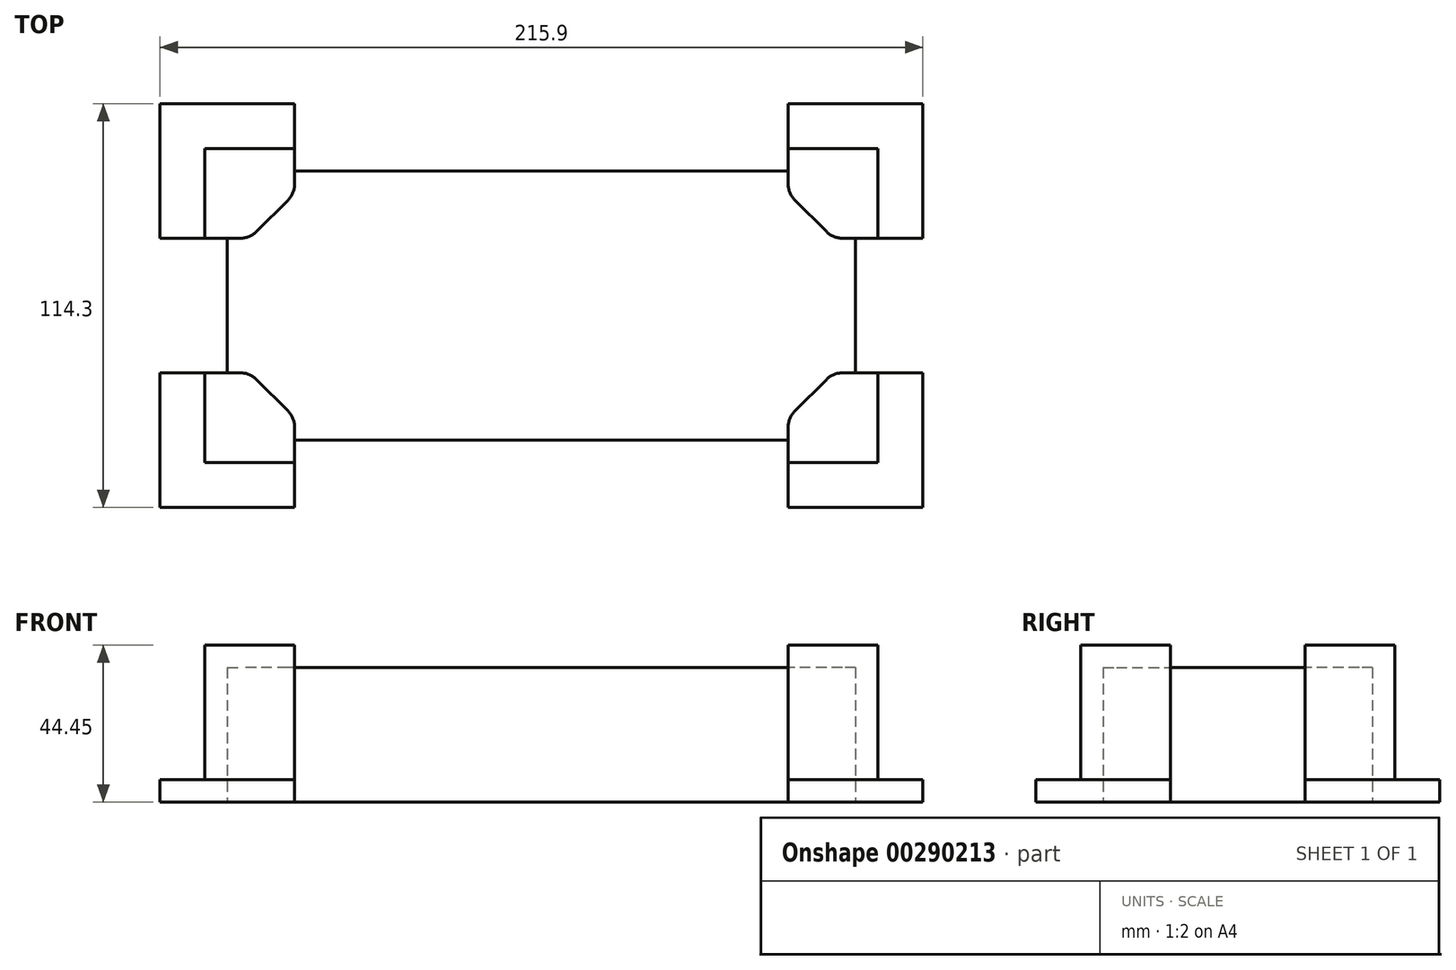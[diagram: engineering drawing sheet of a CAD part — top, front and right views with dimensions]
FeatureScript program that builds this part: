
annotation { "Feature Type Name" : "Feature", "Feature Type Description" : "" }
export const myFeature = defineFeature(function(context is Context, id is Id, definition is map)
    precondition{}
    {
        {
            var Q0;
            Q0=qCreatedBy(makeId("Top.planeOp"),FACE);
            var sketch = newSketch(context, id + "F0", { "sketchPlane" : qUnion([Q0])});
            skLineSegment(sketch, "E0.bottom", {"start": v(88.9, 38.1) * mm, "end": v(-88.9, 38.1) * mm});
            skLineSegment(sketch, "E0.top", {"start": v(88.9, -38.1) * mm, "end": v(-88.9, -38.1) * mm});
            skLineSegment(sketch, "E0.left", {"start": v(88.9, 38.1) * mm, "end": v(88.9, -38.1) * mm});
            skLineSegment(sketch, "E0.right", {"start": v(-88.9, 38.1) * mm, "end": v(-88.9, -38.1) * mm});
            skPoint(sketch, "E0.middle", {"position": v(0, 0) * mm});
            skSolve(sketch);
        }
        {
            var Q0;
            Q0=makeQuery(id+"F0.imprint","IMPRINT",FACE,{"disambiguationData":[TD([[makeQuery(id+"F0.imprint","IMPRINT",EDGE,{"derivedFrom":sQuery(id+"F0.wireOp",EDGE,"E0.bottom")}),1.0]])]});
            extrude(context, id + "F1", {"entities" : qUnion([Q0]), "depth" : 38.1 * mm});
        }
        {
            var Q0;
            Q0=qCreatedBy(makeId("Top.planeOp"),FACE);
            var sketch = newSketch(context, id + "F2", { "sketchPlane" : qUnion([Q0])});
            skLineSegment(sketch, "E1.0.0", {"start": v(-88.9, -38.1) * mm, "end": v(88.9, -38.1) * mm});
            skLineSegment(sketch, "E1.0.1", {"start": v(88.9, -38.1) * mm, "end": v(88.9, 38.1) * mm});
            skLineSegment(sketch, "E1.0.2", {"start": v(88.9, 38.1) * mm, "end": v(-88.9, 38.1) * mm});
            skLineSegment(sketch, "E1.0.3", {"start": v(-88.9, 38.1) * mm, "end": v(-88.9, -38.1) * mm});
            skLineSegment(sketch, "E2", {"start": v(88.9, 0) * mm, "end": v(-88.9, 0) * mm, "construction": true});
            skLineSegment(sketch, "E3", {"start": v(0, -38.1) * mm, "end": v(0, 38.1) * mm, "construction": true});
            skLineSegment(sketch, "E4", {"start": v(-85.18, -19.05) * mm, "end": v(-95.25, -19.05) * mm});
            skLineSegment(sketch, "E5", {"start": v(-95.25, -19.05) * mm, "end": v(-95.25, -44.45) * mm});
            skLineSegment(sketch, "E6", {"start": v(-95.25, -44.45) * mm, "end": v(-69.85, -44.45) * mm});
            skLineSegment(sketch, "E7", {"start": v(-69.85, -44.45) * mm, "end": v(-69.85, -34.38) * mm});
            skLineSegment(sketch, "E8", {"start": v(-71.7, -29.9) * mm, "end": v(-80.7, -20.9) * mm});
            skPoint(sketch, "E9.visualSharp", {"position": v(-82.55, -19.05) * mm});
            skArc(sketch, "E9.filletArc", {"start": v(-80.7, -20.9) * mm, "mid": v(-82.75, -19.53) * mm, "end": v(-85.18, -19.05) * mm});
            skPoint(sketch, "E10.visualSharp", {"position": v(-69.85, -31.75) * mm});
            skArc(sketch, "E10.filletArc", {"start": v(-69.85, -34.38) * mm, "mid": v(-70.33, -31.95) * mm, "end": v(-71.7, -29.9) * mm});
            skLineSegment(sketch, "E11", {"start": v(-95.25, -19.05) * mm, "end": v(-107.95, -19.05) * mm});
            skLineSegment(sketch, "E12", {"start": v(-107.95, -19.05) * mm, "end": v(-107.95, -57.15) * mm});
            skLineSegment(sketch, "E13", {"start": v(-107.95, -57.15) * mm, "end": v(-69.85, -57.15) * mm});
            skLineSegment(sketch, "E14", {"start": v(-69.85, -57.15) * mm, "end": v(-69.85, -44.45) * mm});
            skArc(sketch, "E15.MirrorCS", {"start": v(-80.7, 20.9) * mm, "mid": v(-82.75, 19.53) * mm, "end": v(-85.18, 19.05) * mm});
            skArc(sketch, "E16.MirrorCS", {"start": v(-69.85, 34.38) * mm, "mid": v(-70.33, 31.95) * mm, "end": v(-71.7, 29.9) * mm});
            skLineSegment(sketch, "E17.MirrorCS", {"start": v(-85.18, 19.05) * mm, "end": v(-95.25, 19.05) * mm});
            skLineSegment(sketch, "E18.MirrorCS", {"start": v(-107.95, 19.05) * mm, "end": v(-107.95, 57.15) * mm});
            skPoint(sketch, "E19.MirrorP", {"position": v(-69.85, 31.75) * mm});
            skLineSegment(sketch, "E20.MirrorCS", {"start": v(-95.25, 19.05) * mm, "end": v(-107.95, 19.05) * mm});
            skPoint(sketch, "E21.MirrorP", {"position": v(-82.55, 19.05) * mm});
            skLineSegment(sketch, "E22.MirrorCS", {"start": v(-107.95, 57.15) * mm, "end": v(-69.85, 57.15) * mm});
            skLineSegment(sketch, "E23.MirrorCS", {"start": v(-95.25, 19.05) * mm, "end": v(-95.25, 44.45) * mm});
            skLineSegment(sketch, "E24.MirrorCS", {"start": v(-95.25, 44.45) * mm, "end": v(-69.85, 44.45) * mm});
            skLineSegment(sketch, "E25.MirrorCS", {"start": v(-69.85, 44.45) * mm, "end": v(-69.85, 34.38) * mm});
            skLineSegment(sketch, "E26.MirrorCS", {"start": v(-71.7, 29.9) * mm, "end": v(-80.7, 20.9) * mm});
            skLineSegment(sketch, "E27.MirrorCS", {"start": v(-69.85, 57.15) * mm, "end": v(-69.85, 44.45) * mm});
            skArc(sketch, "E28.MirrorCS", {"start": v(69.85, -34.38) * mm, "mid": v(70.33, -31.95) * mm, "end": v(71.7, -29.9) * mm});
            skArc(sketch, "E29.MirrorCS", {"start": v(69.85, 34.38) * mm, "mid": v(70.33, 31.95) * mm, "end": v(71.7, 29.9) * mm});
            skArc(sketch, "E30.MirrorCS", {"start": v(80.7, -20.9) * mm, "mid": v(82.75, -19.53) * mm, "end": v(85.18, -19.05) * mm});
            skArc(sketch, "E31.MirrorCS", {"start": v(80.7, 20.9) * mm, "mid": v(82.75, 19.53) * mm, "end": v(85.18, 19.05) * mm});
            skLineSegment(sketch, "E32.MirrorCS", {"start": v(71.7, -29.9) * mm, "end": v(80.7, -20.9) * mm});
            skLineSegment(sketch, "E33.MirrorCS", {"start": v(85.18, 19.05) * mm, "end": v(95.25, 19.05) * mm});
            skPoint(sketch, "E34.MirrorP", {"position": v(69.85, -31.75) * mm});
            skLineSegment(sketch, "E35.MirrorCS", {"start": v(71.7, 29.9) * mm, "end": v(80.7, 20.9) * mm});
            skLineSegment(sketch, "E36.MirrorCS", {"start": v(107.95, 57.15) * mm, "end": v(69.85, 57.15) * mm});
            skLineSegment(sketch, "E37.MirrorCS", {"start": v(69.85, 44.45) * mm, "end": v(69.85, 34.38) * mm});
            skLineSegment(sketch, "E38.MirrorCS", {"start": v(69.85, -44.45) * mm, "end": v(69.85, -34.38) * mm});
            skLineSegment(sketch, "E39.MirrorCS", {"start": v(95.25, -44.45) * mm, "end": v(69.85, -44.45) * mm});
            skLineSegment(sketch, "E40.MirrorCS", {"start": v(88.9, 38.1) * mm, "end": v(88.9, -38.1) * mm});
            skPoint(sketch, "E41.MirrorP", {"position": v(82.55, -19.05) * mm});
            skLineSegment(sketch, "E42.MirrorCS", {"start": v(107.95, -57.15) * mm, "end": v(69.85, -57.15) * mm});
            skPoint(sketch, "E43.MirrorP", {"position": v(82.55, 19.05) * mm});
            skLineSegment(sketch, "E44.MirrorCS", {"start": v(69.85, 57.15) * mm, "end": v(69.85, 44.45) * mm});
            skLineSegment(sketch, "E45.MirrorCS", {"start": v(107.95, -19.05) * mm, "end": v(107.95, -57.15) * mm});
            skLineSegment(sketch, "E46.MirrorCS", {"start": v(95.25, 19.05) * mm, "end": v(95.25, 44.45) * mm});
            skLineSegment(sketch, "E47.MirrorCS", {"start": v(95.25, -19.05) * mm, "end": v(107.95, -19.05) * mm});
            skLineSegment(sketch, "E48.MirrorCS", {"start": v(95.25, 19.05) * mm, "end": v(107.95, 19.05) * mm});
            skLineSegment(sketch, "E49.MirrorCS", {"start": v(95.25, 44.45) * mm, "end": v(69.85, 44.45) * mm});
            skPoint(sketch, "E50.MirrorP", {"position": v(69.85, 31.75) * mm});
            skLineSegment(sketch, "E51.MirrorCS", {"start": v(69.85, -57.15) * mm, "end": v(69.85, -44.45) * mm});
            skLineSegment(sketch, "E52.MirrorCS", {"start": v(85.18, -19.05) * mm, "end": v(95.25, -19.05) * mm});
            skLineSegment(sketch, "E53.MirrorCS", {"start": v(107.95, 19.05) * mm, "end": v(107.95, 57.15) * mm});
            skLineSegment(sketch, "E54.MirrorCS", {"start": v(95.25, -19.05) * mm, "end": v(95.25, -44.45) * mm});
            skSolve(sketch);
        }
        {
            var Q0;
            {var subQ0=sQuery(id+"F2.wireOp",EDGE,"E5");Q0=makeQuery(id+"F2.imprint","IMPRINT",FACE,{"disambiguationData":[TD([[makeQuery(id+"F2.imprint","IMPRINT",EDGE,{"derivedFrom":subQ0}),1.0]])]});}
            var Q1;
            Q1=makeQuery(id+"F2.imprint","IMPRINT",FACE,{"disambiguationData":[TD([[makeQuery(id+"F2.imprint","IMPRINT",EDGE,{"derivedFrom":sQuery(id+"F2.wireOp",EDGE,"E8")}),1.0]])]});
            var Q2;
            {var subQ1=sQuery(id+"F2.wireOp",EDGE,"E15.MirrorCS");Q2=makeQuery(id+"F2.imprint","IMPRINT",FACE,{"disambiguationData":[TD([[makeQuery(id+"F2.imprint","IMPRINT",EDGE,{"derivedFrom":subQ1}),-1.0]])]});}
            var Q3;
            {var subQ0=sQuery(id+"F2.wireOp",EDGE,"E23.MirrorCS");Q3=makeQuery(id+"F2.imprint","IMPRINT",FACE,{"disambiguationData":[TD([[makeQuery(id+"F2.imprint","IMPRINT",EDGE,{"derivedFrom":subQ0}),-1.0]])]});}
            var Q4;
            {var subQ0=sQuery(id+"F2.wireOp",EDGE,"E28.MirrorCS");Q4=makeQuery(id+"F2.imprint","IMPRINT",FACE,{"disambiguationData":[TD([[makeQuery(id+"F2.imprint","IMPRINT",EDGE,{"derivedFrom":subQ0}),-1.0]])]});}
            var Q5;
            {var subQ0=sQuery(id+"F2.wireOp",EDGE,"E39.MirrorCS");Q5=makeQuery(id+"F2.imprint","IMPRINT",FACE,{"disambiguationData":[TD([[makeQuery(id+"F2.imprint","IMPRINT",EDGE,{"derivedFrom":subQ0}),-1.0]])]});}
            var Q6;
            {var subQ4=sQuery(id+"F2.wireOp",EDGE,"E29.MirrorCS");Q6=makeQuery(id+"F2.imprint","IMPRINT",FACE,{"disambiguationData":[TD([[makeQuery(id+"F2.imprint","IMPRINT",EDGE,{"derivedFrom":subQ4}),1.0]])]});}
            var Q7;
            {var subQ8=sQuery(id+"F2.wireOp",EDGE,"E46.MirrorCS");Q7=makeQuery(id+"F2.imprint","IMPRINT",FACE,{"disambiguationData":[TD([[makeQuery(id+"F2.imprint","IMPRINT",EDGE,{"derivedFrom":subQ8}),1.0]])]});}
            var Q8;
            Q8=makeQuery(id+"F1.opExtrude","CAP_FACE",FACE,{"disambiguationData":[OSD([sQuery(id+"F0.wireOp",EDGE,"E0.bottom"),sQuery(id+"F0.wireOp",EDGE,"E0.top"),sQuery(id+"F0.wireOp",EDGE,"E0.left"),sQuery(id+"F0.wireOp",EDGE,"E0.right")])],"isStart":false});
            extrude(context, id + "F3", {"entities" : qUnion([Q0, Q1, Q2, Q3, Q4, Q5, Q6, Q7]), "endBound" : BoundingType.UP_TO_SURFACE, "endBoundEntityFace" : qUnion([Q8]), "depth" : 25.4 * mm});
        }
        {
            var Q0;
            Q0=makeQuery(id+"F1.opExtrude","CAP_FACE",FACE,{"disambiguationData":[OSD([sQuery(id+"F0.wireOp",EDGE,"E0.bottom"),sQuery(id+"F0.wireOp",EDGE,"E0.top"),sQuery(id+"F0.wireOp",EDGE,"E0.left"),sQuery(id+"F0.wireOp",EDGE,"E0.right")])],"isStart":false});
            var sketch = newSketch(context, id + "F4", { "sketchPlane" : qUnion([Q0])});
            skLineSegment(sketch, "E55.0.0", {"start": v(-69.85, -38.1) * mm, "end": v(-69.85, -34.38) * mm});
            skArc(sketch, "E55.0.1", {"start": v(-69.85, -34.38) * mm, "mid": v(-70.33, -31.95) * mm, "end": v(-71.7, -29.9) * mm});
            skLineSegment(sketch, "E55.0.2", {"start": v(-71.7, -29.9) * mm, "end": v(-80.7, -20.9) * mm});
            skArc(sketch, "E55.0.3", {"start": v(-80.7, -20.9) * mm, "mid": v(-82.75, -19.53) * mm, "end": v(-85.18, -19.05) * mm});
            skLineSegment(sketch, "E55.0.4", {"start": v(-85.18, -19.05) * mm, "end": v(-88.9, -19.05) * mm});
            skLineSegment(sketch, "E55.0.5", {"start": v(-88.9, -19.05) * mm, "end": v(-88.9, -38.1) * mm});
            skLineSegment(sketch, "E55.0.6", {"start": v(-88.9, -38.1) * mm, "end": v(-69.85, -38.1) * mm});
            skLineSegment(sketch, "E55.1.0", {"start": v(-95.25, -44.45) * mm, "end": v(-69.85, -44.45) * mm});
            skLineSegment(sketch, "E55.1.1", {"start": v(-69.85, -44.45) * mm, "end": v(-69.85, -38.1) * mm});
            skLineSegment(sketch, "E55.1.2", {"start": v(-69.85, -38.1) * mm, "end": v(-88.9, -38.1) * mm});
            skLineSegment(sketch, "E55.1.3", {"start": v(-88.9, -38.1) * mm, "end": v(-88.9, -19.05) * mm});
            skLineSegment(sketch, "E55.1.4", {"start": v(-88.9, -19.05) * mm, "end": v(-95.25, -19.05) * mm});
            skLineSegment(sketch, "E55.1.5", {"start": v(-95.25, -19.05) * mm, "end": v(-95.25, -44.45) * mm});
            skLineSegment(sketch, "E55.2.0", {"start": v(-69.85, 34.38) * mm, "end": v(-69.85, 38.1) * mm});
            skLineSegment(sketch, "E55.2.1", {"start": v(-69.85, 38.1) * mm, "end": v(-88.9, 38.1) * mm});
            skLineSegment(sketch, "E55.2.2", {"start": v(-88.9, 38.1) * mm, "end": v(-88.9, 19.05) * mm});
            skLineSegment(sketch, "E55.2.3", {"start": v(-88.9, 19.05) * mm, "end": v(-85.18, 19.05) * mm});
            skArc(sketch, "E55.2.4", {"start": v(-85.18, 19.05) * mm, "mid": v(-82.75, 19.53) * mm, "end": v(-80.7, 20.9) * mm});
            skLineSegment(sketch, "E55.2.5", {"start": v(-80.7, 20.9) * mm, "end": v(-71.7, 29.9) * mm});
            skArc(sketch, "E55.2.6", {"start": v(-71.7, 29.9) * mm, "mid": v(-70.33, 31.95) * mm, "end": v(-69.85, 34.38) * mm});
            skLineSegment(sketch, "E55.3.0", {"start": v(-69.85, 44.45) * mm, "end": v(-95.25, 44.45) * mm});
            skLineSegment(sketch, "E55.3.1", {"start": v(-95.25, 44.45) * mm, "end": v(-95.25, 19.05) * mm});
            skLineSegment(sketch, "E55.3.2", {"start": v(-95.25, 19.05) * mm, "end": v(-88.9, 19.05) * mm});
            skLineSegment(sketch, "E55.3.3", {"start": v(-88.9, 19.05) * mm, "end": v(-88.9, 38.1) * mm});
            skLineSegment(sketch, "E55.3.4", {"start": v(-88.9, 38.1) * mm, "end": v(-69.85, 38.1) * mm});
            skLineSegment(sketch, "E55.3.5", {"start": v(-69.85, 38.1) * mm, "end": v(-69.85, 44.45) * mm});
            skLineSegment(sketch, "E55.4.0", {"start": v(88.9, -19.05) * mm, "end": v(85.18, -19.05) * mm});
            skArc(sketch, "E55.4.1", {"start": v(85.18, -19.05) * mm, "mid": v(82.75, -19.53) * mm, "end": v(80.7, -20.9) * mm});
            skLineSegment(sketch, "E55.4.2", {"start": v(80.7, -20.9) * mm, "end": v(71.7, -29.9) * mm});
            skArc(sketch, "E55.4.3", {"start": v(71.7, -29.9) * mm, "mid": v(70.33, -31.95) * mm, "end": v(69.85, -34.38) * mm});
            skLineSegment(sketch, "E55.4.4", {"start": v(69.85, -34.38) * mm, "end": v(69.85, -38.1) * mm});
            skLineSegment(sketch, "E55.4.5", {"start": v(69.85, -38.1) * mm, "end": v(88.9, -38.1) * mm});
            skLineSegment(sketch, "E55.4.6", {"start": v(88.9, -38.1) * mm, "end": v(88.9, -19.05) * mm});
            skArc(sketch, "E55.5.0", {"start": v(80.7, 20.9) * mm, "mid": v(82.75, 19.53) * mm, "end": v(85.18, 19.05) * mm});
            skLineSegment(sketch, "E55.5.1", {"start": v(85.18, 19.05) * mm, "end": v(88.9, 19.05) * mm});
            skLineSegment(sketch, "E55.5.2", {"start": v(88.9, 19.05) * mm, "end": v(88.9, 38.1) * mm});
            skLineSegment(sketch, "E55.5.3", {"start": v(88.9, 38.1) * mm, "end": v(69.85, 38.1) * mm});
            skLineSegment(sketch, "E55.5.4", {"start": v(69.85, 38.1) * mm, "end": v(69.85, 34.38) * mm});
            skArc(sketch, "E55.5.5", {"start": v(69.85, 34.38) * mm, "mid": v(70.33, 31.95) * mm, "end": v(71.7, 29.9) * mm});
            skLineSegment(sketch, "E55.5.6", {"start": v(71.7, 29.9) * mm, "end": v(80.7, 20.9) * mm});
            skLineSegment(sketch, "E55.6.0", {"start": v(95.25, 44.45) * mm, "end": v(69.85, 44.45) * mm});
            skLineSegment(sketch, "E55.6.1", {"start": v(69.85, 44.45) * mm, "end": v(69.85, 38.1) * mm});
            skLineSegment(sketch, "E55.6.2", {"start": v(69.85, 38.1) * mm, "end": v(88.9, 38.1) * mm});
            skLineSegment(sketch, "E55.6.3", {"start": v(88.9, 38.1) * mm, "end": v(88.9, 19.05) * mm});
            skLineSegment(sketch, "E55.6.4", {"start": v(88.9, 19.05) * mm, "end": v(95.25, 19.05) * mm});
            skLineSegment(sketch, "E55.6.5", {"start": v(95.25, 19.05) * mm, "end": v(95.25, 44.45) * mm});
            skLineSegment(sketch, "E55.7.0", {"start": v(95.25, -19.05) * mm, "end": v(88.9, -19.05) * mm});
            skLineSegment(sketch, "E55.7.1", {"start": v(88.9, -19.05) * mm, "end": v(88.9, -38.1) * mm});
            skLineSegment(sketch, "E55.7.2", {"start": v(88.9, -38.1) * mm, "end": v(69.85, -38.1) * mm});
            skLineSegment(sketch, "E55.7.3", {"start": v(69.85, -38.1) * mm, "end": v(69.85, -44.45) * mm});
            skLineSegment(sketch, "E55.7.4", {"start": v(69.85, -44.45) * mm, "end": v(95.25, -44.45) * mm});
            skLineSegment(sketch, "E55.7.5", {"start": v(95.25, -44.45) * mm, "end": v(95.25, -19.05) * mm});
            skSolve(sketch);
        }
        {
            var Q0;
            Q0 = qSketchRegion(id + "F4", true);
            extrude(context, id + "F5", {"entities" : qUnion([Q0]), "operationType" : NewBodyOperationType.ADD, "depth" : 6.35 * mm});
        }
        {
            var Q0;
            Q0=makeQuery(id+"F2.imprint","IMPRINT",FACE,{"disambiguationData":[TD([[makeQuery(id+"F2.imprint","IMPRINT",EDGE,{"derivedFrom":sQuery(id+"F2.wireOp",EDGE,"E36.MirrorCS")}),1.0]])]});
            var Q1;
            Q1=makeQuery(id+"F2.imprint","IMPRINT",FACE,{"disambiguationData":[TD([[makeQuery(id+"F2.imprint","IMPRINT",EDGE,{"derivedFrom":sQuery(id+"F2.wireOp",EDGE,"E18.MirrorCS")}),-1.0]])]});
            var Q2;
            Q2=makeQuery(id+"F2.imprint","IMPRINT",FACE,{"disambiguationData":[TD([[makeQuery(id+"F2.imprint","IMPRINT",EDGE,{"derivedFrom":sQuery(id+"F2.wireOp",EDGE,"E39.MirrorCS")}),1.0]])]});
            var Q3;
            Q3=makeQuery(id+"F2.imprint","IMPRINT",FACE,{"disambiguationData":[TD([[makeQuery(id+"F2.imprint","IMPRINT",EDGE,{"derivedFrom":sQuery(id+"F2.wireOp",EDGE,"E5")}),-1.0]])]});
            extrude(context, id + "F6", {"entities" : qUnion([Q0, Q1, Q2, Q3]), "operationType" : NewBodyOperationType.ADD, "depth" : 6.35 * mm});
        }
    });
